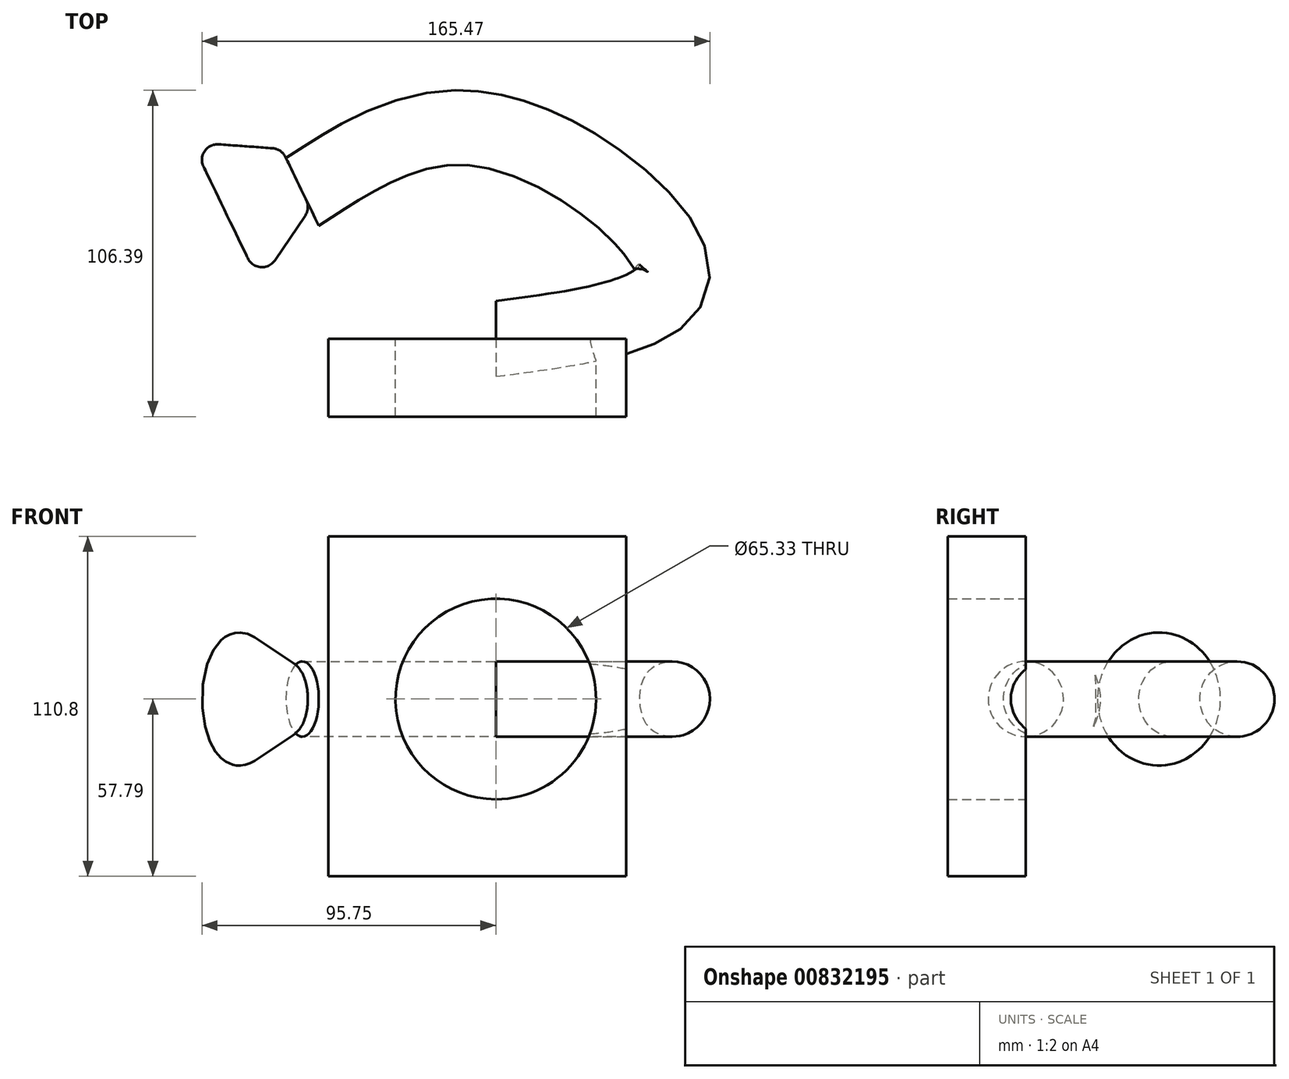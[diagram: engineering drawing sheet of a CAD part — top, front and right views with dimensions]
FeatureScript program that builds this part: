
annotation { "Feature Type Name" : "Feature", "Feature Type Description" : "" }
export const myFeature = defineFeature(function(context is Context, id is Id, definition is map)
    precondition{}
    {
        {
            var Q0;
            Q0=qCreatedBy(makeId("Front.planeOp"),FACE);
            var sketch = newSketch(context, id + "F0", { "sketchPlane" : qUnion([Q0])});
            skLineSegment(sketch, "E0.bottom", {"start": v(-54.53, 53.01) * mm, "end": v(42.46, 53.01) * mm});
            skLineSegment(sketch, "E0.top", {"start": v(-54.53, -57.8) * mm, "end": v(42.46, -57.8) * mm});
            skLineSegment(sketch, "E0.left", {"start": v(-54.53, 53.01) * mm, "end": v(-54.53, -57.8) * mm});
            skLineSegment(sketch, "E0.right", {"start": v(42.46, 53.01) * mm, "end": v(42.46, -57.8) * mm});
            skCircle(sketch, "E1", {"center": v(0, 0) * mm, "radius": 32.67 * mm});
            skSolve(sketch);
        }
        {
            var Q0;
            Q0 = qSketchRegion(id + "F0", true);
            extrude(context, id + "F1", {"entities" : qUnion([Q0]), "depth" : 25.4 * mm, "offsetDistance" : 25.4 * mm});
        }
        {
            var Q0;
            Q0=qCreatedBy(makeId("Top.planeOp"),FACE);
            var sketch = newSketch(context, id + "F2", { "sketchPlane" : qUnion([Q0])});
            skFitSpline(sketch, "E2", {"points": [v(0, 0) * mm, v(57.48, 20.73) * mm, v(0, 67.46) * mm, v(-63.03, 47.82) * mm], "startDerivative": vector(266.66, 35.06) * mm, "endDerivative": vector(-173.83, -114.14) * mm});
            skSolve(sketch);
        }
        {
            var Q0;
            Q0=qCreatedBy(makeId("Right.planeOp"),FACE);
            var sketch = newSketch(context, id + "F3", { "sketchPlane" : qUnion([Q0])});
            skCircle(sketch, "E3", {"center": v(0, 0) * mm, "radius": 12.27 * mm});
            skSolve(sketch);
        }
        {
            var Q0;
            Q0=makeQuery(id+"F3.imprint","IMPRINT",FACE,{"disambiguationData":[TD([[makeQuery(id+"F3.imprint","IMPRINT",EDGE,{"derivedFrom":sQuery(id+"F3.wireOp",EDGE,"E3")}),1.0]])]});
            var Q1;
            Q1=sQuery(id+"F2.wireOp",EDGE,"E2");
            sweep(context, id + "F4", {"operationType" : NewBodyOperationType.ADD, "profiles" : qUnion([Q0]), "path" : qUnion([Q1])});
        }
        {
            var Q0;
            Q0=makeQuery(id+"F4.opSweep","CAP_FACE",FACE,{"disambiguationData":[OSD([sQuery(id+"F2.wireOp",VERTEX,"E2.end"),sQuery(id+"F3.wireOp",EDGE,"E3")])],"isStart":false});
            cPlane(context, id + "F5", {"entities" : qUnion([Q0]), "cplaneType" : CPlaneType.OFFSET, "offset" : 25.4 * mm, "width" : 152.4 * mm, "height" : 152.4 * mm});
        }
        {
            var Q0;
            Q0=qCreatedBy(id+"F5.planeOp",FACE);
            var sketch = newSketch(context, id + "F6", { "sketchPlane" : qUnion([Q0])});
            skCircle(sketch, "E4", {"center": v(-75.35, 0) * mm, "radius": 25.4 * mm});
            skSolve(sketch);
        }
        {
            var Q0;
            Q0=makeQuery(id+"F6.imprint","IMPRINT",FACE,{"disambiguationData":[TD([[makeQuery(id+"F6.imprint","IMPRINT",EDGE,{"derivedFrom":sQuery(id+"F6.wireOp",EDGE,"E4")}),1.0]])]});
            var Q1;
            Q1=sQuery(id+"F6.wireOp",EDGE,"E4");
            var Q2;
            Q2=makeQuery(id+"F4.opSweep","CAP_FACE",FACE,{"disambiguationData":[OSD([sQuery(id+"F2.wireOp",VERTEX,"E2.end"),sQuery(id+"F3.wireOp",EDGE,"E3")])],"isStart":false});
            extrude(context, id + "F7", {"entities" : qUnion([Q0]), "surfaceOperationType" : NewSurfaceOperationType.ADD, "surfaceEntities" : qUnion([Q1]), "endBound" : BoundingType.UP_TO_SURFACE, "oppositeDirection" : true, "depth" : 25.4 * mm, "endBoundEntityFace" : qUnion([Q2]), "offsetDistance" : 25.4 * mm, "hasDraft" : true, "draftAngle" : 30 * degree, "draftPullDirection" : true});
        }
        {
            var Q0;
            Q0=makeQuery(id+"F7.opExtrude","SWEPT_FACE",FACE,{"disambiguationData":[OSD([sQuery(id+"F6.wireOp",EDGE,"E4")])]});
            fillet(context, id + "F8", {"entities" : qUnion([Q0]), "radius" : 5.08 * mm, "tangentPropagation" : true, "allowEdgeOverflow" : false});
        }
    });
